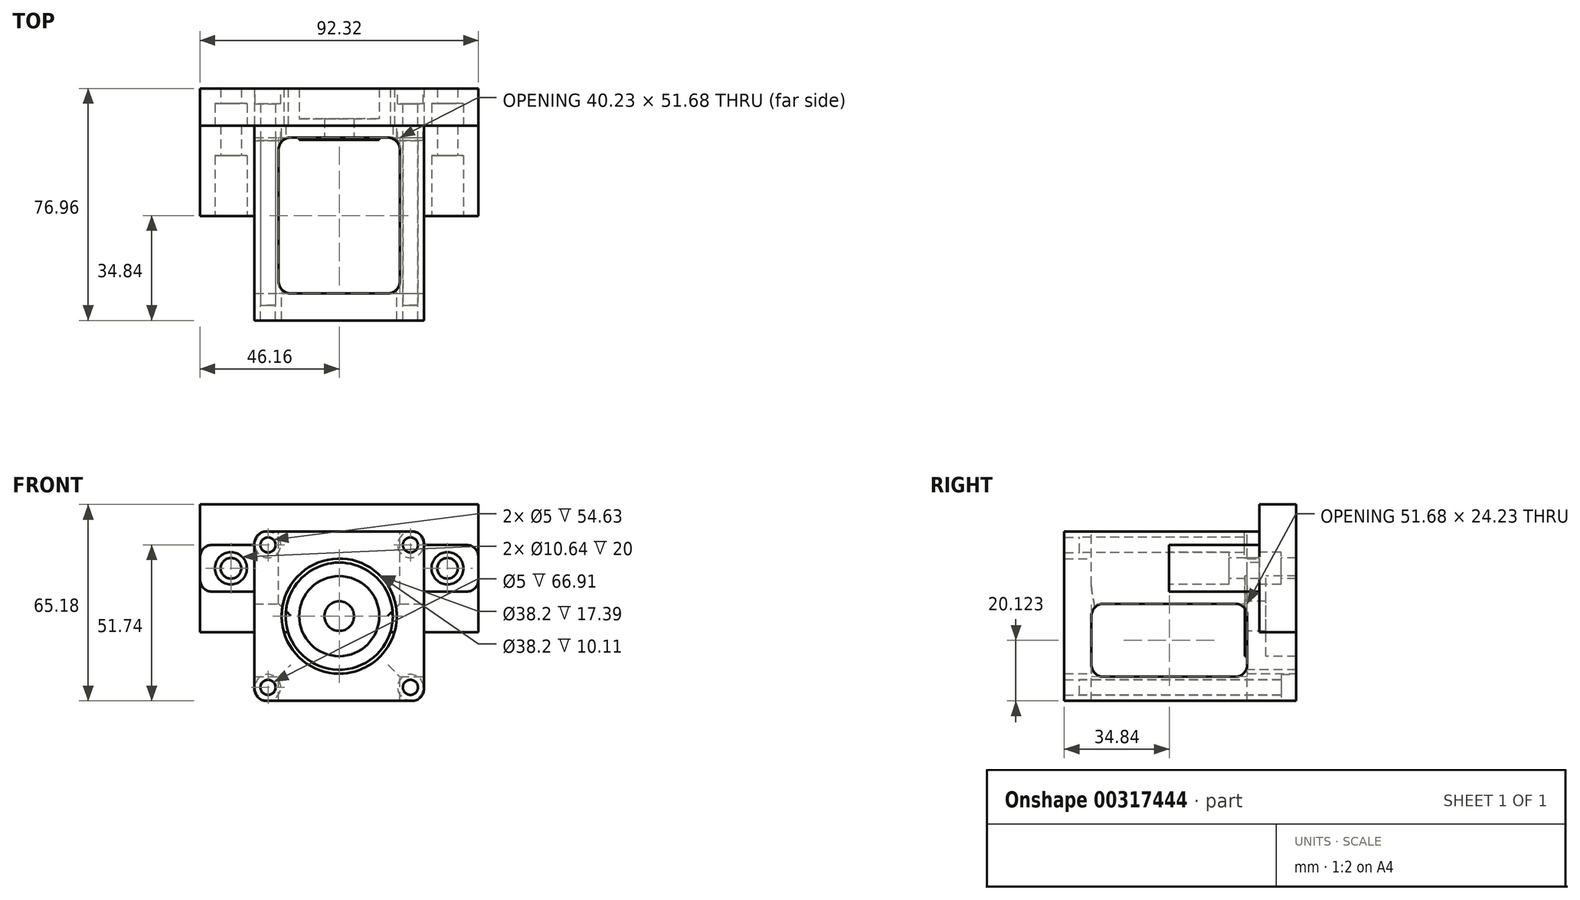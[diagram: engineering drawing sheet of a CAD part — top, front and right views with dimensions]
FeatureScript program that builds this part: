
annotation { "Feature Type Name" : "Feature", "Feature Type Description" : "" }
export const myFeature = defineFeature(function(context is Context, id is Id, definition is map)
    precondition{}
    {
        {
            var Q0;
            Q0=qCreatedBy(makeId("Front.planeOp"),FACE);
            var sketch = newSketch(context, id + "F0", { "sketchPlane" : qUnion([Q0])});
            skLineSegment(sketch, "E0.rect.bottom", {"start": v(-28.11, 28.11) * mm, "end": v(28.12, 28.11) * mm});
            skLineSegment(sketch, "E0.rect.top", {"start": v(-28.12, -28.11) * mm, "end": v(28.11, -28.11) * mm});
            skLineSegment(sketch, "E0.rect.left", {"start": v(-28.11, 28.12) * mm, "end": v(-28.12, -28.11) * mm});
            skLineSegment(sketch, "E0.rect.right", {"start": v(28.12, 28.11) * mm, "end": v(28.11, -28.11) * mm});
            skPoint(sketch, "E0.rect.middle", {"position": v(0, 0) * mm});
            skCircle(sketch, "E1", {"center": v(0, 0) * mm, "radius": 19.1 * mm});
            skCircle(sketch, "E2", {"center": v(0, 0) * mm, "radius": 3.98 * mm});
            skCircle(sketch, "E3", {"center": v(-23.62, 23.62) * mm, "radius": 2.52 * mm});
            skCircle(sketch, "E4", {"center": v(23.62, 23.62) * mm, "radius": 2.52 * mm});
            skCircle(sketch, "E5", {"center": v(23.62, -23.62) * mm, "radius": 2.52 * mm});
            skCircle(sketch, "E6", {"center": v(-23.62, -23.62) * mm, "radius": 2.52 * mm});
            skLineSegment(sketch, "E7.rect.bottom", {"start": v(-23.62, 23.62) * mm, "end": v(23.62, 23.62) * mm, "construction": true});
            skLineSegment(sketch, "E7.rect.top", {"start": v(-23.62, -23.62) * mm, "end": v(23.62, -23.62) * mm, "construction": true});
            skLineSegment(sketch, "E7.rect.left", {"start": v(-23.62, 23.62) * mm, "end": v(-23.62, -23.62) * mm, "construction": true});
            skLineSegment(sketch, "E7.rect.right", {"start": v(23.62, 23.62) * mm, "end": v(23.62, -23.62) * mm, "construction": true});
            skCircle(sketch, "E8", {"center": v(0, 0) * mm, "radius": 5.38 * mm});
            skSolve(sketch);
        }
        {
            var Q0;
            Q0=qCreatedBy(makeId("Front.planeOp"),FACE);
            var sketch = newSketch(context, id + "F1", { "sketchPlane" : qUnion([Q0])});
            skLineSegment(sketch, "E9.bottom", {"start": v(46.15, 37.06) * mm, "end": v(-46.16, 37.06) * mm});
            skLineSegment(sketch, "E9.top", {"start": v(46.16, -5.28) * mm, "end": v(-46.16, -5.28) * mm});
            skLineSegment(sketch, "E9.left", {"start": v(46.15, 37.06) * mm, "end": v(46.16, -5.28) * mm});
            skLineSegment(sketch, "E9.right", {"start": v(-46.16, 37.06) * mm, "end": v(-46.16, -5.28) * mm});
            skCircle(sketch, "E10", {"center": v(0, 0) * mm, "radius": 13.28 * mm});
            skCircle(sketch, "E11", {"center": v(-35.92, 15.87) * mm, "radius": 3.41 * mm});
            skCircle(sketch, "E12", {"center": v(35.91, 15.87) * mm, "radius": 3.41 * mm});
            skCircle(sketch, "E13", {"center": v(-35.92, 15.87) * mm, "radius": 5.32 * mm});
            skCircle(sketch, "E14", {"center": v(35.91, 15.87) * mm, "radius": 5.32 * mm});
            skSolve(sketch);
        }
        {
            var Q0;
            Q0=qCreatedBy(makeId("Front.planeOp"),FACE);
            var sketch = newSketch(context, id + "F2", { "sketchPlane" : qUnion([Q0])});
            skCircle(sketch, "E15", {"center": v(0, 0) * mm, "radius": 4.91 * mm});
            skCircle(sketch, "E16", {"center": v(0, 0) * mm, "radius": 13.28 * mm});
            skCircle(sketch, "E17", {"center": v(0, 0) * mm, "radius": 17.77 * mm});
            skSolve(sketch);
        }
        {
            var Q0;
            Q0=makeQuery(id+"F1.imprint","IMPRINT",FACE,{"disambiguationData":[TD([[makeQuery(id+"F1.imprint","IMPRINT",EDGE,{"derivedFrom":sQuery(id+"F1.wireOp",EDGE,"E9.bottom")}),1.0]])]});
            extrude(context, id + "F3", {"entities" : qUnion([Q0]), "oppositeDirection" : true, "depth" : 42.28 * mm, "hasSecondDirection" : true, "secondDirectionOppositeDirection" : true, "secondDirectionDepth" : 30 * mm});
        }
        {
            var Q0;
            Q0=qSketchRegion(id+"F0",true);
            extrude(context, id + "F4", {"entities" : qUnion([Q0]), "depth" : 34.68 * mm, "hasSecondDirection" : true, "secondDirectionOppositeDirection" : false, "secondDirectionDepth" : 29.68 * mm});
        }
        {
            var Q0;
            Q0=qCreatedBy(makeId("Front.planeOp"),FACE);
            var sketch = newSketch(context, id + "F5", { "sketchPlane" : qUnion([Q0])});
            skLineSegment(sketch, "E18.bottom", {"start": v(-28.11, 28.11) * mm, "end": v(28.12, 28.11) * mm});
            skLineSegment(sketch, "E18.top", {"start": v(-28.11, -5.28) * mm, "end": v(28.12, -5.28) * mm});
            skLineSegment(sketch, "E18.left", {"start": v(-28.11, 28.11) * mm, "end": v(-28.11, -5.28) * mm});
            skLineSegment(sketch, "E18.right", {"start": v(28.12, 28.12) * mm, "end": v(28.12, -5.28) * mm});
            skLineSegment(sketch, "E19.bottom", {"start": v(-28.11, -5.28) * mm, "end": v(28.11, -5.28) * mm});
            skLineSegment(sketch, "E19.top", {"start": v(-28.12, -28.11) * mm, "end": v(28.11, -28.11) * mm});
            skLineSegment(sketch, "E19.left", {"start": v(-28.11, -5.28) * mm, "end": v(-28.11, -28.11) * mm});
            skLineSegment(sketch, "E19.right", {"start": v(28.11, -5.28) * mm, "end": v(28.11, -28.11) * mm});
            skCircle(sketch, "E20", {"center": v(0, 0) * mm, "radius": 19.1 * mm});
            skCircle(sketch, "E21", {"center": v(-23.62, 23.62) * mm, "radius": 2.5 * mm});
            skCircle(sketch, "E22", {"center": v(23.62, 23.62) * mm, "radius": 2.5 * mm});
            skCircle(sketch, "E23", {"center": v(-23.62, -23.62) * mm, "radius": 2.5 * mm});
            skCircle(sketch, "E24", {"center": v(23.62, -23.62) * mm, "radius": 2.52 * mm});
            skLineSegment(sketch, "E25.bottom", {"start": v(46.15, 23.62) * mm, "end": v(28.11, 23.62) * mm});
            skLineSegment(sketch, "E25.top", {"start": v(46.15, 8.12) * mm, "end": v(28.12, 8.12) * mm});
            skLineSegment(sketch, "E25.left", {"start": v(46.15, 23.62) * mm, "end": v(46.15, 8.12) * mm});
            skLineSegment(sketch, "E25.right", {"start": v(28.12, 23.62) * mm, "end": v(28.12, 8.12) * mm});
            skLineSegment(sketch, "E26.bottom", {"start": v(-28.11, 23.62) * mm, "end": v(-46.16, 23.62) * mm});
            skLineSegment(sketch, "E26.top", {"start": v(-28.11, 8.12) * mm, "end": v(-46.16, 8.12) * mm});
            skLineSegment(sketch, "E26.left", {"start": v(-28.11, 23.62) * mm, "end": v(-28.11, 8.12) * mm});
            skLineSegment(sketch, "E26.right", {"start": v(-46.16, 23.62) * mm, "end": v(-46.16, 8.12) * mm});
            skCircle(sketch, "E27", {"center": v(35.91, 15.87) * mm, "radius": 3.41 * mm});
            skCircle(sketch, "E28", {"center": v(35.91, 15.87) * mm, "radius": 5.32 * mm});
            skCircle(sketch, "E29", {"center": v(-35.92, 15.87) * mm, "radius": 5.32 * mm});
            skCircle(sketch, "E30", {"center": v(-35.92, 15.87) * mm, "radius": 3.41 * mm});
            skSolve(sketch);
        }
        {
            var Q0;
            Q0=makeQuery(id+"F5.imprint","IMPRINT",FACE,{"disambiguationData":[TD([[makeQuery(id+"F5.imprint","IMPRINT",EDGE,{"derivedFrom":sQuery(id+"F5.wireOp",EDGE,"E19.top")}),1.0]])]});
            var Q1;
            Q1=makeQuery(id+"F3.opExtrude","CAP_FACE",FACE,{"disambiguationData":[OSD([sQuery(id+"F1.wireOp",EDGE,"E9.bottom"),sQuery(id+"F1.wireOp",EDGE,"E9.top"),sQuery(id+"F1.wireOp",EDGE,"E9.left"),sQuery(id+"F1.wireOp",EDGE,"E9.right"),sQuery(id+"F1.wireOp",EDGE,"E10"),sQuery(id+"F1.wireOp",EDGE,"E13"),sQuery(id+"F1.wireOp",EDGE,"E14")])],"isStart":false});
            extrude(context, id + "F6", {"entities" : qUnion([Q0]), "oppositeDirection" : true, "endBoundEntityFace" : qUnion([Q1]), "depth" : 42.28 * mm, "hasSecondDirection" : true, "secondDirectionOppositeDirection" : false, "secondDirectionDepth" : 29.68 * mm});
        }
        {
            var Q0;
            Q0=makeQuery(id+"F5.imprint","IMPRINT",FACE,{"disambiguationData":[TD([[makeQuery(id+"F5.imprint","IMPRINT",EDGE,{"derivedFrom":sQuery(id+"F5.wireOp",EDGE,"E18.bottom")}),-1.0]])]});
            var Q1;
            Q1=makeQuery(id+"F3.opExtrude","CAP_FACE",FACE,{"disambiguationData":[OSD([sQuery(id+"F1.wireOp",EDGE,"E9.bottom"),sQuery(id+"F1.wireOp",EDGE,"E9.top"),sQuery(id+"F1.wireOp",EDGE,"E9.left"),sQuery(id+"F1.wireOp",EDGE,"E9.right"),sQuery(id+"F1.wireOp",EDGE,"E10"),sQuery(id+"F1.wireOp",EDGE,"E13"),sQuery(id+"F1.wireOp",EDGE,"E14")])],"isStart":true});
            extrude(context, id + "F7", {"entities" : qUnion([Q0]), "operationType" : NewBodyOperationType.ADD, "oppositeDirection" : true, "endBoundEntityFace" : qUnion([Q1]), "offsetDistance" : 25 * mm, "depth" : 30 * mm, "hasSecondDirection" : true, "secondDirectionOppositeDirection" : false, "secondDirectionDepth" : 29.68 * mm});
        }
        {
            var Q0;
            Q0=makeQuery(id+"F2.imprint","IMPRINT",FACE,{"disambiguationData":[TD([[makeQuery(id+"F2.imprint","IMPRINT",EDGE,{"derivedFrom":sQuery(id+"F2.wireOp",EDGE,"E16")}),-1.0]])]});
            extrude(context, id + "F8", {"entities" : qUnion([Q0]), "operationType" : NewBodyOperationType.ADD, "oppositeDirection" : true, "offsetDistance" : 25 * mm, "depth" : 42.28 * mm, "hasSecondDirection" : true, "secondDirectionOppositeDirection" : true, "secondDirectionDepth" : 14.32 * mm});
        }
        {
            var Q0;
            Q0=makeQuery(id+"F1.imprint","IMPRINT",FACE,{"disambiguationData":[TD([[makeQuery(id+"F1.imprint","IMPRINT",EDGE,{"derivedFrom":sQuery(id+"F1.wireOp",EDGE,"E12")}),-1.0]])]});
            var Q1;
            Q1=makeQuery(id+"F1.imprint","IMPRINT",FACE,{"disambiguationData":[TD([[makeQuery(id+"F1.imprint","IMPRINT",EDGE,{"derivedFrom":sQuery(id+"F1.wireOp",EDGE,"E11")}),-1.0]])]});
            var Q2;
            Q2 = qSketchRegion(id + "F20", true);
            extrude(context, id + "F9", {"entities" : qUnion([Q0, Q1, Q2]), "operationType" : NewBodyOperationType.ADD, "oppositeDirection" : true, "offsetDistance" : 25 * mm, "depth" : 42.28 * mm, "hasSecondDirection" : true, "secondDirectionOppositeDirection" : true, "secondDirectionDepth" : 37.28 * mm});
        }
        {
            var Q0;
            Q0=makeQuery(id+"F5.imprint","IMPRINT",FACE,{"disambiguationData":[TD([[makeQuery(id+"F5.imprint","IMPRINT",EDGE,{"derivedFrom":sQuery(id+"F5.wireOp",EDGE,"E25.bottom")}),1.0]])]});
            var Q1;
            Q1=makeQuery(id+"F5.imprint","IMPRINT",FACE,{"disambiguationData":[TD([[makeQuery(id+"F5.imprint","IMPRINT",EDGE,{"derivedFrom":sQuery(id+"F5.wireOp",EDGE,"E26.bottom")}),1.0]])]});
            extrude(context, id + "F10", {"entities" : qUnion([Q0, Q1]), "operationType" : NewBodyOperationType.ADD, "oppositeDirection" : true, "depth" : 30 * mm});
        }
        {
            var Q0;
            Q0=makeQuery(id+"F1.imprint","IMPRINT",FACE,{"disambiguationData":[TD([[makeQuery(id+"F1.imprint","IMPRINT",EDGE,{"derivedFrom":sQuery(id+"F1.wireOp",EDGE,"E12")}),-1.0]])]});
            var Q1;
            Q1=makeQuery(id+"F1.imprint","IMPRINT",FACE,{"disambiguationData":[TD([[makeQuery(id+"F1.imprint","IMPRINT",EDGE,{"derivedFrom":sQuery(id+"F1.wireOp",EDGE,"E11")}),-1.0]])]});
            extrude(context, id + "F11", {"entities" : qUnion([Q0, Q1]), "operationType" : NewBodyOperationType.ADD, "oppositeDirection" : true, "depth" : 30 * mm, "hasSecondDirection" : true, "secondDirectionOppositeDirection" : true, "secondDirectionDepth" : 20 * mm});
        }
        {
            var Q0;
            Q0=makeQuery(id+"F10.opExtrude","SWEPT_EDGE",EDGE,{"disambiguationData":[OSD([sQuery(id+"F5.wireOp",EDGE,"E26.bottom"),sQuery(id+"F5.wireOp",EDGE,"E26.right")])]});
            var Q1;
            Q1=makeQuery(id+"F10.opExtrude","SWEPT_EDGE",EDGE,{"disambiguationData":[OSD([sQuery(id+"F5.wireOp",EDGE,"E26.top"),sQuery(id+"F5.wireOp",EDGE,"E26.right")])]});
            var Q2;
            Q2=makeQuery(id+"F6.opExtrude","SWEPT_EDGE",EDGE,{"disambiguationData":[OSD([sQuery(id+"F5.wireOp",EDGE,"E19.top"),sQuery(id+"F5.wireOp",EDGE,"E19.left")])]});
            var Q3;
            Q3=makeQuery(id+"F6.opExtrude","SWEPT_EDGE",EDGE,{"disambiguationData":[OSD([sQuery(id+"F5.wireOp",EDGE,"E19.top"),sQuery(id+"F5.wireOp",EDGE,"E19.right")])]});
            var Q4;
            Q4=makeQuery(id+"F10.opExtrude","SWEPT_EDGE",EDGE,{"disambiguationData":[OSD([sQuery(id+"F5.wireOp",EDGE,"E25.top"),sQuery(id+"F5.wireOp",EDGE,"E25.left")])]});
            var Q5;
            Q5=makeQuery(id+"F10.opExtrude","SWEPT_EDGE",EDGE,{"disambiguationData":[OSD([sQuery(id+"F5.wireOp",EDGE,"E25.bottom"),sQuery(id+"F5.wireOp",EDGE,"E25.left")])]});
            var Q6;
            Q6=makeQuery(id+"F7.opExtrude","SWEPT_EDGE",EDGE,{"disambiguationData":[OSD([sQuery(id+"F5.wireOp",EDGE,"E18.bottom"),sQuery(id+"F5.wireOp",EDGE,"E18.right")])]});
            var Q7;
            Q7=makeQuery(id+"F7.opExtrude","SWEPT_EDGE",EDGE,{"disambiguationData":[OSD([sQuery(id+"F5.wireOp",EDGE,"E18.bottom"),sQuery(id+"F5.wireOp",EDGE,"E18.left")])]});
            fillet(context, id + "F12", {"entities" : qUnion([Q0, Q1, Q2, Q3, Q4, Q5, Q6, Q7]), "radius" : 4 * mm, "tangentPropagation" : true, "allowEdgeOverflow" : false});
        }
        {
            var Q0;
            Q0=makeQuery(id+"F7.opExtrude","SWEPT_FACE",FACE,{"disambiguationData":[OSD([sQuery(id+"F5.wireOp",EDGE,"E18.bottom")])]});
            var sketch = newSketch(context, id + "F13", { "sketchPlane" : qUnion([Q0])});
            skLineSegment(sketch, "E31.bottom", {"start": v(-16.11, 26) * mm, "end": v(16.11, 26) * mm});
            skLineSegment(sketch, "E31.top", {"start": v(-16.11, -25.68) * mm, "end": v(16.11, -25.68) * mm});
            skLineSegment(sketch, "E31.left", {"start": v(-20.11, 22) * mm, "end": v(-20.11, -21.68) * mm});
            skLineSegment(sketch, "E31.right", {"start": v(20.11, 22) * mm, "end": v(20.11, -21.68) * mm});
            skPoint(sketch, "E32.visualSharp", {"position": v(-20.11, 26) * mm});
            skArc(sketch, "E32.filletArc", {"start": v(-16.11, 26) * mm, "mid": v(-18.94, 24.83) * mm, "end": v(-20.11, 22) * mm});
            skPoint(sketch, "E33.visualSharp", {"position": v(-20.11, -25.68) * mm});
            skArc(sketch, "E33.filletArc", {"start": v(-20.11, -21.68) * mm, "mid": v(-18.94, -24.5) * mm, "end": v(-16.11, -25.68) * mm});
            skPoint(sketch, "E34.visualSharp", {"position": v(20.11, -25.68) * mm});
            skArc(sketch, "E34.filletArc", {"start": v(16.11, -25.68) * mm, "mid": v(18.94, -24.5) * mm, "end": v(20.11, -21.68) * mm});
            skPoint(sketch, "E35.visualSharp", {"position": v(20.11, 26) * mm});
            skArc(sketch, "E35.filletArc", {"start": v(20.11, 22) * mm, "mid": v(18.94, 24.83) * mm, "end": v(16.11, 26) * mm});
            skSolve(sketch);
        }
        {
            var Q0;
            Q0=qSketchRegion(id+"F13",true);
            var Q1;
            {var subQ0=sQuery(id+"F5.wireOp",EDGE,"E26.left");var subQ1=sQuery(id+"F5.wireOp",EDGE,"E25.right");Q1=makeQuery(id+"F11.boolean.opBoolean","MERGE",FACE,{"derivedFrom":[makeQuery(id+"F10.boolean.opBoolean","MERGE",FACE,{"derivedFrom":[makeQuery(id+"F7.opExtrude","CAP_FACE",FACE,{"disambiguationData":[OSD([sQuery(id+"F5.wireOp",EDGE,"E18.bottom"),sQuery(id+"F5.wireOp",EDGE,"E18.left"),sQuery(id+"F5.wireOp",EDGE,"E18.right"),sQuery(id+"F5.wireOp",EDGE,"E19.bottom"),sQuery(id+"F5.wireOp",EDGE,"E20"),sQuery(id+"F5.wireOp",EDGE,"E21"),sQuery(id+"F5.wireOp",EDGE,"E22"),subQ1,subQ0])],"isStart":false}),makeQuery(id+"F10.opExtrude","CAP_FACE",FACE,{"disambiguationData":[OSD([sQuery(id+"F5.wireOp",EDGE,"E25.bottom"),sQuery(id+"F5.wireOp",EDGE,"E25.top"),sQuery(id+"F5.wireOp",EDGE,"E25.left"),subQ1,sQuery(id+"F5.wireOp",EDGE,"E28")])],"isStart":false}),makeQuery(id+"F10.opExtrude","CAP_FACE",FACE,{"disambiguationData":[OSD([sQuery(id+"F5.wireOp",EDGE,"E26.bottom"),sQuery(id+"F5.wireOp",EDGE,"E26.top"),subQ0,sQuery(id+"F5.wireOp",EDGE,"E26.right"),sQuery(id+"F5.wireOp",EDGE,"E29")])],"isStart":false})]}),makeQuery(id+"F11.opExtrude","CAP_FACE",FACE,{"disambiguationData":[OSD([sQuery(id+"F1.wireOp",EDGE,"E11"),sQuery(id+"F1.wireOp",EDGE,"E13")])],"isStart":false}),makeQuery(id+"F11.opExtrude","CAP_FACE",FACE,{"disambiguationData":[OSD([sQuery(id+"F1.wireOp",EDGE,"E12"),sQuery(id+"F1.wireOp",EDGE,"E14")])],"isStart":false})]});}
            extrude(context, id + "F14", {"entities" : qUnion([Q0]), "operationType" : NewBodyOperationType.REMOVE, "endBound" : BoundingType.THROUGH_ALL, "oppositeDirection" : true, "endBoundEntityFace" : qUnion([Q1]), "depth" : 25 * mm});
        }
        {
            var Q0;
            {var subQ1=sQuery(id+"F5.wireOp",EDGE,"E25.right");var subQ6=sQuery(id+"F5.wireOp",EDGE,"E18.right");var subQ15=sQuery(id+"F5.wireOp",EDGE,"E19.right");var subQ17=sQuery(id+"F5.wireOp",EDGE,"E19.top");Q0=makeQuery(id+"F10.boolean.opBoolean","SPLIT",FACE,{"disambiguationData":[TD([makeQuery(id+"F6.opExtrude","SWEPT_FACE",FACE,{"disambiguationData":[OSD([subQ17])]})])],"derivedFrom":makeQuery(id+"F7.boolean.opBoolean","MERGE",FACE,{"derivedFrom":[makeQuery(id+"F6.opExtrude","SWEPT_FACE",FACE,{"disambiguationData":[OSD([subQ15])]}),makeQuery(id+"F7.opExtrude","SWEPT_FACE",FACE,{"disambiguationData":[OSD([subQ6,subQ1])]})]})});}
            var sketch = newSketch(context, id + "F15", { "sketchPlane" : qUnion([Q0])});
            skLineSegment(sketch, "E36.bottom", {"start": v(-21.68, 4.12) * mm, "end": v(22, 4.12) * mm});
            skLineSegment(sketch, "E36.top", {"start": v(-21.68, -20.11) * mm, "end": v(22, -20.11) * mm});
            skLineSegment(sketch, "E36.left", {"start": v(-25.68, 0.12) * mm, "end": v(-25.68, -16.11) * mm});
            skLineSegment(sketch, "E36.right", {"start": v(26, 0.12) * mm, "end": v(26, -16.11) * mm});
            skPoint(sketch, "E37.visualSharp", {"position": v(-25.68, 4.12) * mm});
            skArc(sketch, "E37.filletArc", {"start": v(-21.68, 4.12) * mm, "mid": v(-24.5, 2.95) * mm, "end": v(-25.68, 0.12) * mm});
            skPoint(sketch, "E38.visualSharp", {"position": v(26, 4.12) * mm});
            skArc(sketch, "E38.filletArc", {"start": v(26, 0.12) * mm, "mid": v(24.83, 2.95) * mm, "end": v(22, 4.12) * mm});
            skPoint(sketch, "E39.visualSharp", {"position": v(26, -20.11) * mm});
            skArc(sketch, "E39.filletArc", {"start": v(22, -20.11) * mm, "mid": v(24.83, -18.94) * mm, "end": v(26, -16.11) * mm});
            skPoint(sketch, "E40.visualSharp", {"position": v(-25.68, -20.11) * mm});
            skArc(sketch, "E40.filletArc", {"start": v(-25.68, -16.11) * mm, "mid": v(-24.5, -18.94) * mm, "end": v(-21.68, -20.11) * mm});
            skSolve(sketch);
        }
        {
            var Q0;
            Q0=qSketchRegion(id+"F15",true);
            extrude(context, id + "F16", {"entities" : qUnion([Q0]), "operationType" : NewBodyOperationType.REMOVE, "endBound" : BoundingType.THROUGH_ALL, "oppositeDirection" : true, "depth" : 25 * mm});
        }
        {
            var Q0;
            Q0=makeQuery(id+"F2.imprint","IMPRINT",FACE,{"disambiguationData":[TD([[makeQuery(id+"F2.imprint","IMPRINT",EDGE,{"derivedFrom":sQuery(id+"F2.wireOp",EDGE,"E15")}),-1.0]])]});
            extrude(context, id + "F17", {"entities" : qUnion([Q0]), "operationType" : NewBodyOperationType.ADD, "oppositeDirection" : true, "depth" : 32.22 * mm, "hasSecondDirection" : true, "secondDirectionOppositeDirection" : true, "secondDirectionDepth" : 25.23 * mm});
        }
        {
            var Q0;
            Q0=makeQuery(id+"F6.opExtrude","CAP_FACE",FACE,{"disambiguationData":[OSD([sQuery(id+"F5.wireOp",EDGE,"E19.bottom"),sQuery(id+"F5.wireOp",EDGE,"E19.top"),sQuery(id+"F5.wireOp",EDGE,"E19.left"),sQuery(id+"F5.wireOp",EDGE,"E19.right"),sQuery(id+"F5.wireOp",EDGE,"E20"),sQuery(id+"F5.wireOp",EDGE,"E23"),sQuery(id+"F5.wireOp",EDGE,"E24")])],"isStart":false});
            var sketch = newSketch(context, id + "F18", { "sketchPlane" : qUnion([Q0])});
            skCircle(sketch, "E41", {"center": v(-23.62, -23.62) * mm, "radius": 4.28 * mm});
            skCircle(sketch, "E42", {"center": v(23.66, -23.62) * mm, "radius": 4.28 * mm});
            skSolve(sketch);
        }
        {
            var Q0;
            Q0 = qSketchRegion(id + "F18", true);
            extrude(context, id + "F19", {"entities" : qUnion([Q0]), "operationType" : NewBodyOperationType.REMOVE, "oppositeDirection" : true, "depth" : 5.05 * mm, "offsetDistance" : 25 * mm});
        }
        {
            var Q0;
            {var subQ0=sQuery(id+"F5.wireOp",EDGE,"E26.left");var subQ1=sQuery(id+"F5.wireOp",EDGE,"E25.right");Q0=makeQuery(id+"F11.boolean.opBoolean","MERGE",FACE,{"derivedFrom":[makeQuery(id+"F10.boolean.opBoolean","MERGE",FACE,{"derivedFrom":[makeQuery(id+"F7.opExtrude","CAP_FACE",FACE,{"disambiguationData":[OSD([sQuery(id+"F5.wireOp",EDGE,"E18.bottom"),sQuery(id+"F5.wireOp",EDGE,"E18.left"),sQuery(id+"F5.wireOp",EDGE,"E18.right"),sQuery(id+"F5.wireOp",EDGE,"E19.bottom"),sQuery(id+"F5.wireOp",EDGE,"E20"),sQuery(id+"F5.wireOp",EDGE,"E21"),sQuery(id+"F5.wireOp",EDGE,"E22"),subQ1,subQ0])],"isStart":false}),makeQuery(id+"F10.opExtrude","CAP_FACE",FACE,{"disambiguationData":[OSD([sQuery(id+"F5.wireOp",EDGE,"E25.bottom"),sQuery(id+"F5.wireOp",EDGE,"E25.top"),sQuery(id+"F5.wireOp",EDGE,"E25.left"),subQ1,sQuery(id+"F5.wireOp",EDGE,"E28")])],"isStart":false}),makeQuery(id+"F10.opExtrude","CAP_FACE",FACE,{"disambiguationData":[OSD([sQuery(id+"F5.wireOp",EDGE,"E26.bottom"),sQuery(id+"F5.wireOp",EDGE,"E26.top"),subQ0,sQuery(id+"F5.wireOp",EDGE,"E26.right"),sQuery(id+"F5.wireOp",EDGE,"E29")])],"isStart":false})]}),makeQuery(id+"F11.opExtrude","CAP_FACE",FACE,{"disambiguationData":[OSD([sQuery(id+"F1.wireOp",EDGE,"E11"),sQuery(id+"F1.wireOp",EDGE,"E13")])],"isStart":false}),makeQuery(id+"F11.opExtrude","CAP_FACE",FACE,{"disambiguationData":[OSD([sQuery(id+"F1.wireOp",EDGE,"E12"),sQuery(id+"F1.wireOp",EDGE,"E14")])],"isStart":false})]});}
            var sketch = newSketch(context, id + "F20", { "sketchPlane" : qUnion([Q0])});
            skCircle(sketch, "E43", {"center": v(-23.62, 23.62) * mm, "radius": 4.28 * mm});
            skCircle(sketch, "E44", {"center": v(23.66, 23.65) * mm, "radius": 4.28 * mm});
            skSolve(sketch);
        }
        {
            var Q0;
            Q0=makeQuery(id+"F20.imprint","IMPRINT",FACE,{"disambiguationData":[TD([[makeQuery(id+"F20.imprint","IMPRINT",EDGE,{"derivedFrom":sQuery(id+"F20.wireOp",EDGE,"E44")}),1.0]])]});
            var Q1;
            Q1=makeQuery(id+"F20.imprint","IMPRINT",FACE,{"disambiguationData":[TD([[makeQuery(id+"F20.imprint","IMPRINT",EDGE,{"derivedFrom":sQuery(id+"F20.wireOp",EDGE,"E43")}),1.0]])]});
            var Q2;
            Q2=sQuery(id+"F20.wireOp",EDGE,"E43");
            var Q3;
            Q3=sQuery(id+"F20.wireOp",EDGE,"E44");
            extrude(context, id + "F21", {"entities" : qUnion([Q0, Q1]), "operationType" : NewBodyOperationType.REMOVE, "surfaceEntities" : qUnion([Q2, Q3]), "oppositeDirection" : true, "depth" : 5.05 * mm, "offsetDistance" : 25 * mm});
        }
    });
